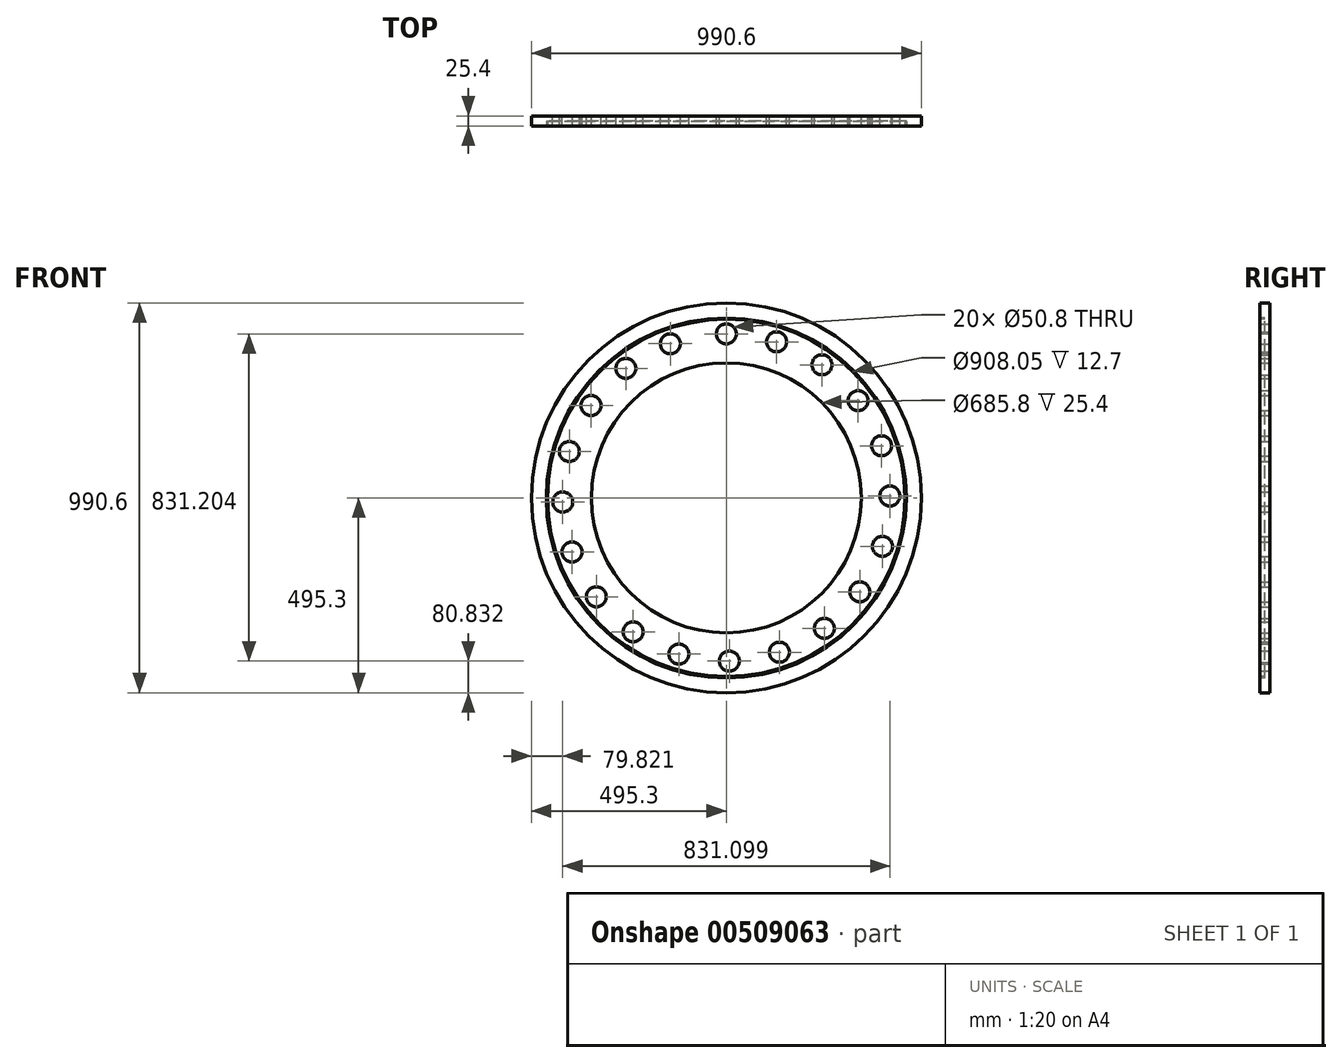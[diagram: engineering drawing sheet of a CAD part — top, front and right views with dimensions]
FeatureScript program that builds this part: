
annotation { "Feature Type Name" : "Feature", "Feature Type Description" : "" }
export const myFeature = defineFeature(function(context is Context, id is Id, definition is map)
    precondition{}
    {
        {
            var Q0;
            Q0=qCreatedBy(makeId("Front.planeOp"),FACE);
            var sketch = newSketch(context, id + "F0", { "sketchPlane" : qUnion([Q0])});
            skCircle(sketch, "E0", {"center": v(0, 0) * mm, "radius": 495.3 * mm});
            skCircle(sketch, "E1", {"center": v(0, 0) * mm, "radius": 342.9 * mm});
            skCircle(sketch, "E2", {"center": v(0, 416.74) * mm, "radius": 25.4 * mm});
            skCircle(sketch, "E3.1.0", {"center": v(127.71, 396.63) * mm, "radius": 25.4 * mm});
            skCircle(sketch, "E3.2.0", {"center": v(243.07, 338.25) * mm, "radius": 25.4 * mm});
            skCircle(sketch, "E3.3.0", {"center": v(334.9, 247.25) * mm, "radius": 25.4 * mm});
            skCircle(sketch, "E3.4.0", {"center": v(394.34, 132.44) * mm, "radius": 25.4 * mm});
            skCircle(sketch, "E3.5.0", {"center": v(415.62, 4.92) * mm, "radius": 25.4 * mm});
            skCircle(sketch, "E3.6.0", {"center": v(396.69, -122.97) * mm, "radius": 25.4 * mm});
            skCircle(sketch, "E3.7.0", {"center": v(339.37, -238.86) * mm, "radius": 25.4 * mm});
            skCircle(sketch, "E3.8.0", {"center": v(249.22, -331.53) * mm, "radius": 25.4 * mm});
            skCircle(sketch, "E3.9.0", {"center": v(134.96, -392.02) * mm, "radius": 25.4 * mm});
            skCircle(sketch, "E3.10.0", {"center": v(7.64, -414.47) * mm, "radius": 25.4 * mm});
            skCircle(sketch, "E3.11.0", {"center": v(-120.42, -396.71) * mm, "radius": 25.4 * mm});
            skCircle(sketch, "E3.12.0", {"center": v(-236.83, -340.46) * mm, "radius": 25.4 * mm});
            skCircle(sketch, "E3.13.0", {"center": v(-330.33, -251.17) * mm, "radius": 25.4 * mm});
            skCircle(sketch, "E3.14.0", {"center": v(-391.86, -137.46) * mm, "radius": 25.4 * mm});
            skCircle(sketch, "E3.15.0", {"center": v(-415.48, -10.35) * mm, "radius": 25.4 * mm});
            skCircle(sketch, "E3.16.0", {"center": v(-398.9, 117.86) * mm, "radius": 25.4 * mm});
            skCircle(sketch, "E3.17.0", {"center": v(-343.72, 234.79) * mm, "radius": 25.4 * mm});
            skCircle(sketch, "E3.18.0", {"center": v(-255.29, 329.1) * mm, "radius": 25.4 * mm});
            skCircle(sketch, "E3.19.0", {"center": v(-142.16, 391.67) * mm, "radius": 25.4 * mm});
            skPoint(sketch, "E3.center", {"position": v(0, 1.1) * mm});
            skLineSegment(sketch, "E3.anchor1", {"start": v(0, 1.1) * mm, "end": v(0, 416.74) * mm, "construction": true});
            skLineSegment(sketch, "E3.anchor2", {"start": v(0, 1.1) * mm, "end": v(-142.16, 391.67) * mm, "construction": true});
            skSolve(sketch);
        }
        {
            var Q0;
            Q0=makeQuery(id+"F0.imprint","IMPRINT",FACE,{"disambiguationData":[TD([[makeQuery(id+"F0.imprint","IMPRINT",EDGE,{"derivedFrom":sQuery(id+"F0.wireOp",EDGE,"E0")}),1.0]])]});
            extrude(context, id + "F1", {"entities" : qUnion([Q0]), "depth" : 25.4 * mm});
        }
        {
            var Q0;
            Q0=makeQuery(id+"F1.opExtrude","CAP_FACE",FACE,{"disambiguationData":[OSD([sQuery(id+"F0.wireOp",EDGE,"E0"),sQuery(id+"F0.wireOp",EDGE,"E1"),sQuery(id+"F0.wireOp",EDGE,"E2"),sQuery(id+"F0.wireOp",EDGE,"E3.1.0"),sQuery(id+"F0.wireOp",EDGE,"E3.2.0"),sQuery(id+"F0.wireOp",EDGE,"E3.3.0"),sQuery(id+"F0.wireOp",EDGE,"E3.4.0"),sQuery(id+"F0.wireOp",EDGE,"E3.5.0"),sQuery(id+"F0.wireOp",EDGE,"E3.6.0"),sQuery(id+"F0.wireOp",EDGE,"E3.7.0"),sQuery(id+"F0.wireOp",EDGE,"E3.8.0"),sQuery(id+"F0.wireOp",EDGE,"E3.9.0"),sQuery(id+"F0.wireOp",EDGE,"E3.10.0"),sQuery(id+"F0.wireOp",EDGE,"E3.11.0"),sQuery(id+"F0.wireOp",EDGE,"E3.12.0"),sQuery(id+"F0.wireOp",EDGE,"E3.13.0"),sQuery(id+"F0.wireOp",EDGE,"E3.14.0"),sQuery(id+"F0.wireOp",EDGE,"E3.15.0"),sQuery(id+"F0.wireOp",EDGE,"E3.16.0"),sQuery(id+"F0.wireOp",EDGE,"E3.17.0"),sQuery(id+"F0.wireOp",EDGE,"E3.18.0"),sQuery(id+"F0.wireOp",EDGE,"E3.19.0")])],"isStart":false});
            var sketch = newSketch(context, id + "F2", { "sketchPlane" : qUnion([Q0])});
            skCircle(sketch, "E4", {"center": v(0, 0) * mm, "radius": 381 * mm});
            skCircle(sketch, "E5", {"center": v(0, 0) * mm, "radius": 419.1 * mm});
            skCircle(sketch, "E6", {"center": v(0, 0) * mm, "radius": 457.2 * mm});
            skCircle(sketch, "E7", {"center": v(0, 0) * mm, "radius": 384.18 * mm});
            skCircle(sketch, "E8", {"center": v(0, 0) * mm, "radius": 454.03 * mm});
            skLineSegment(sketch, "E9", {"start": v(-405, -212.14) * mm, "end": v(-337.53, -176.74) * mm});
            skLineSegment(sketch, "E10", {"start": v(-340.48, -171.11) * mm, "end": v(-337.53, -176.74) * mm});
            skLineSegment(sketch, "E11", {"start": v(-407.91, -206.5) * mm, "end": v(-340.48, -171.11) * mm});
            skLineSegment(sketch, "E12", {"start": v(-407.91, 206.5) * mm, "end": v(-339.93, 172.08) * mm});
            skLineSegment(sketch, "E13", {"start": v(-405, 212.14) * mm, "end": v(-337.01, 177.72) * mm});
            skLineSegment(sketch, "E14", {"start": v(409.49, -203.35) * mm, "end": v(341.47, -168.98) * mm});
            skLineSegment(sketch, "E15", {"start": v(406.62, -209.02) * mm, "end": v(338.61, -174.65) * mm});
            skLineSegment(sketch, "E16", {"start": v(409.49, 203.35) * mm, "end": v(341.47, 168.98) * mm});
            skLineSegment(sketch, "E17", {"start": v(338.61, 174.65) * mm, "end": v(406.62, 209.02) * mm});
            skLineSegment(sketch, "E18", {"start": v(-405, -212.14) * mm, "end": v(-407.91, -206.5) * mm});
            skLineSegment(sketch, "E19", {"start": v(-337.53, -176.74) * mm, "end": v(-340.48, -171.11) * mm});
            skLineSegment(sketch, "E20", {"start": v(-407.91, 206.5) * mm, "end": v(-405, 212.14) * mm});
            skLineSegment(sketch, "E21", {"start": v(-339.93, 172.08) * mm, "end": v(-337.01, 177.72) * mm});
            skLineSegment(sketch, "E22", {"start": v(341.47, 168.98) * mm, "end": v(338.61, 174.65) * mm});
            skLineSegment(sketch, "E23", {"start": v(409.49, 203.35) * mm, "end": v(406.62, 209.02) * mm});
            skLineSegment(sketch, "E24", {"start": v(338.61, -174.65) * mm, "end": v(341.47, -168.98) * mm});
            skLineSegment(sketch, "E25", {"start": v(406.62, -209.02) * mm, "end": v(409.49, -203.35) * mm});
            skSolve(sketch);
        }
        {
            var Q0;
            Q0 = qSketchRegion(id + "F2", true);
            extrude(context, id + "F3", {"entities" : qUnion([Q0]), "oppositeDirection" : true, "depth" : 12.7 * mm});
        }
    });
